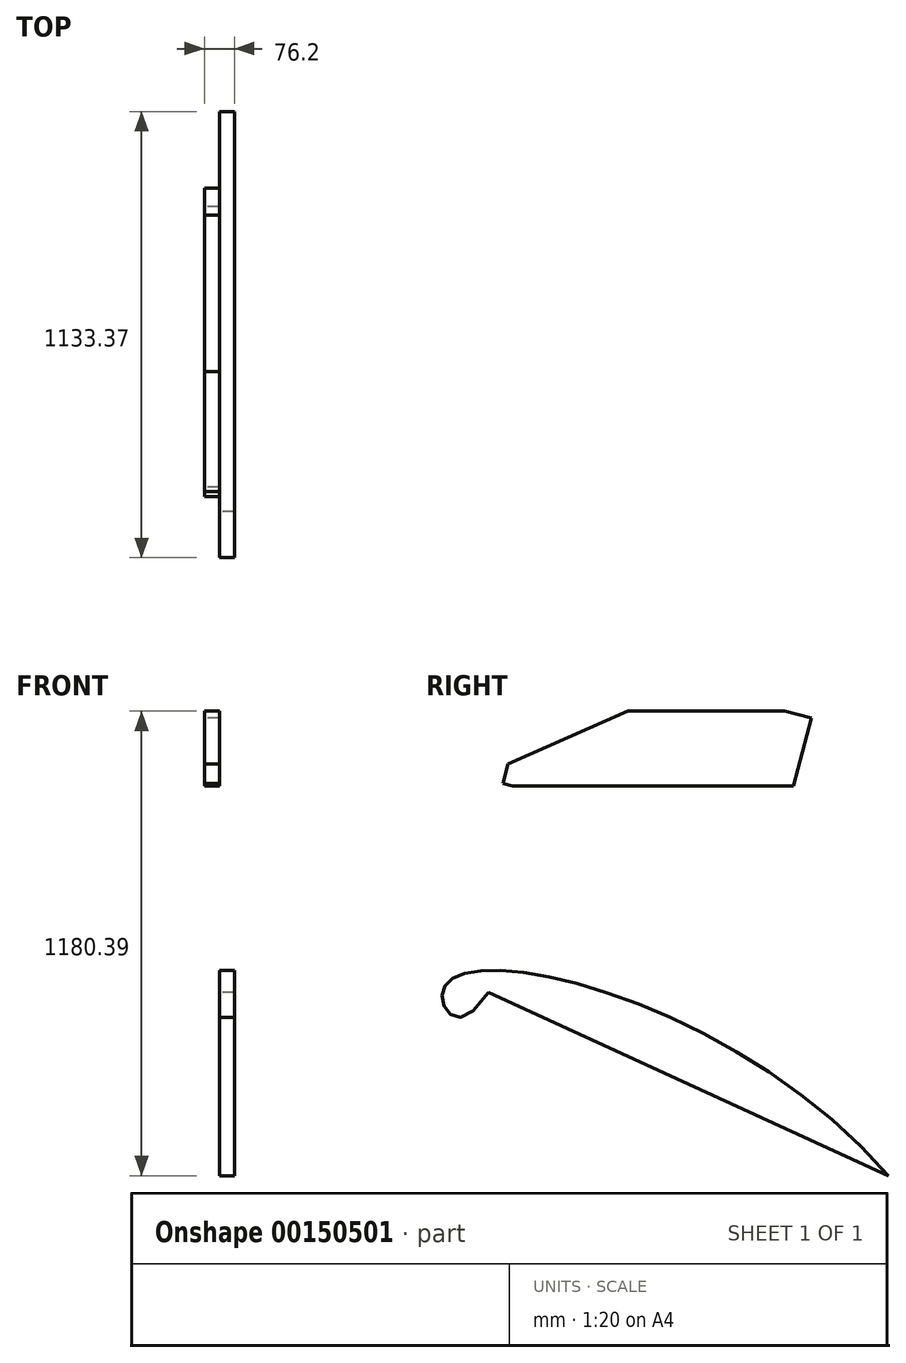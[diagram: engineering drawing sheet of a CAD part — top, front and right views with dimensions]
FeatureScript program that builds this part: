
annotation { "Feature Type Name" : "Feature", "Feature Type Description" : "" }
export const myFeature = defineFeature(function(context is Context, id is Id, definition is map)
    precondition{}
    {
        {
            var Q0;
            Q0=qCreatedBy(makeId("Right.planeOp"),FACE);
            var sketch = newSketch(context, id + "F0", { "sketchPlane" : qUnion([Q0])});
            skLineSegment(sketch, "E0.bottom", {"start": v(-365.94, -508.58) * mm, "end": v(417.42, -508.58) * mm});
            skLineSegment(sketch, "E0.top", {"start": v(-365.94, -318.08) * mm, "end": v(417.42, -318.08) * mm});
            skLineSegment(sketch, "E0.left", {"start": v(-365.94, -508.58) * mm, "end": v(-365.94, -318.08) * mm, "construction": true});
            skLineSegment(sketch, "E0.right", {"start": v(417.42, -508.58) * mm, "end": v(417.42, -318.08) * mm, "construction": true});
            skPoint(sketch, "E1.firstSnap0", {"position": v(25.74, -508.58) * mm});
            skLineSegment(sketch, "E2", {"start": v(371.38, -508.58) * mm, "end": v(417.42, -508.58) * mm, "construction": true});
            skLineSegment(sketch, "E3", {"start": v(-365.94, -502) * mm, "end": v(-341.4, -508.58) * mm});
            skLineSegment(sketch, "E4", {"start": v(-365.94, -502) * mm, "end": v(-352.8, -452.94) * mm});
            skLineSegment(sketch, "E5", {"start": v(-352.8, -452.94) * mm, "end": v(-48.44, -318.08) * mm});
            skLineSegment(sketch, "E6", {"start": v(-48.44, -318.08) * mm, "end": v(-365.94, -318.08) * mm, "construction": true});
            skLineSegment(sketch, "E7", {"start": v(-365.94, -318.08) * mm, "end": v(-352.8, -452.94) * mm, "construction": true});
            skLineSegment(sketch, "E8", {"start": v(417.42, -318.08) * mm, "end": v(417.42, -336.04) * mm});
            skPoint(sketch, "E8.endSnap0", {"position": v(435.2, -336.04) * mm});
            skLineSegment(sketch, "E9", {"start": v(417.42, -336.04) * mm, "end": v(371.38, -508.58) * mm});
            skLineSegment(sketch, "E10", {"start": v(417.42, -318.08) * mm, "end": v(349.16, -318.08) * mm, "construction": true});
            skLineSegment(sketch, "E11", {"start": v(349.16, -318.08) * mm, "end": v(417.42, -336.04) * mm});
            skSolve(sketch);
        }
        {
            var Q0;
            {var subQ0=sQuery(id+"F0.wireOp",EDGE,"E3");Q0=makeQuery(id+"F0.imprint","IMPRINT",FACE,{"disambiguationData":[TD([[makeQuery(id+"F0.imprint","IMPRINT",EDGE,{"derivedFrom":subQ0}),1.0]])]});}
            extrude(context, id + "F1", {"entities" : qUnion([Q0]), "depth" : 38.1 * mm});
        }
        {
            var Q0;
            Q0=makeQuery(id+"F1.opExtrude","SWEPT_FACE",FACE,{"disambiguationData":[OSD([sQuery(id+"F0.wireOp",EDGE,"E0.top")])]});
            var sketch = newSketch(context, id + "F2", { "sketchPlane" : qUnion([Q0])});
            skLineSegment(sketch, "E12", {"start": v(17.02, -48.44) * mm, "end": v(17.02, -23.04) * mm, "construction": true});
            skLineSegment(sketch, "E13", {"start": v(17.02, -23.04) * mm, "end": v(38.1, -23.04) * mm, "construction": true});
            skSolve(sketch);
        }
        {
            var Q0;
            Q0=makeQuery(id+"F1.opExtrude","CAP_FACE",FACE,{"disambiguationData":[OSD([sQuery(id+"F0.wireOp",EDGE,"E0.bottom"),sQuery(id+"F0.wireOp",EDGE,"E0.top"),sQuery(id+"F0.wireOp",EDGE,"E3"),sQuery(id+"F0.wireOp",EDGE,"E4"),sQuery(id+"F0.wireOp",EDGE,"E5"),sQuery(id+"F0.wireOp",EDGE,"E9"),sQuery(id+"F0.wireOp",EDGE,"E11")])],"isStart":false});
            var sketch = newSketch(context, id + "F3", { "sketchPlane" : qUnion([Q0])});
            skFitSpline(sketch, "E14", {"points": [v(612.73, -1498.47) * mm, v(-519.29, -1029.68) * mm, v(-403.27, -1032.88) * mm], "startDerivative": vector(-1520.47, 1769.95) * mm, "endDerivative": vector(935, 1508.42) * mm});
            skLineSegment(sketch, "E15", {"start": v(-403.27, -1032.88) * mm, "end": v(612.73, -1498.47) * mm});
            skSolve(sketch);
        }
        {
            var Q0;
            Q0=makeQuery(id+"F3.imprint","IMPRINT",FACE,{"disambiguationData":[TD([[makeQuery(id+"F3.imprint","IMPRINT",EDGE,{"derivedFrom":sQuery(id+"F3.wireOp",EDGE,"E14")}),1.0]])]});
            extrude(context, id + "F4", {"entities" : qUnion([Q0]), "depth" : 38.1 * mm});
        }
    });
